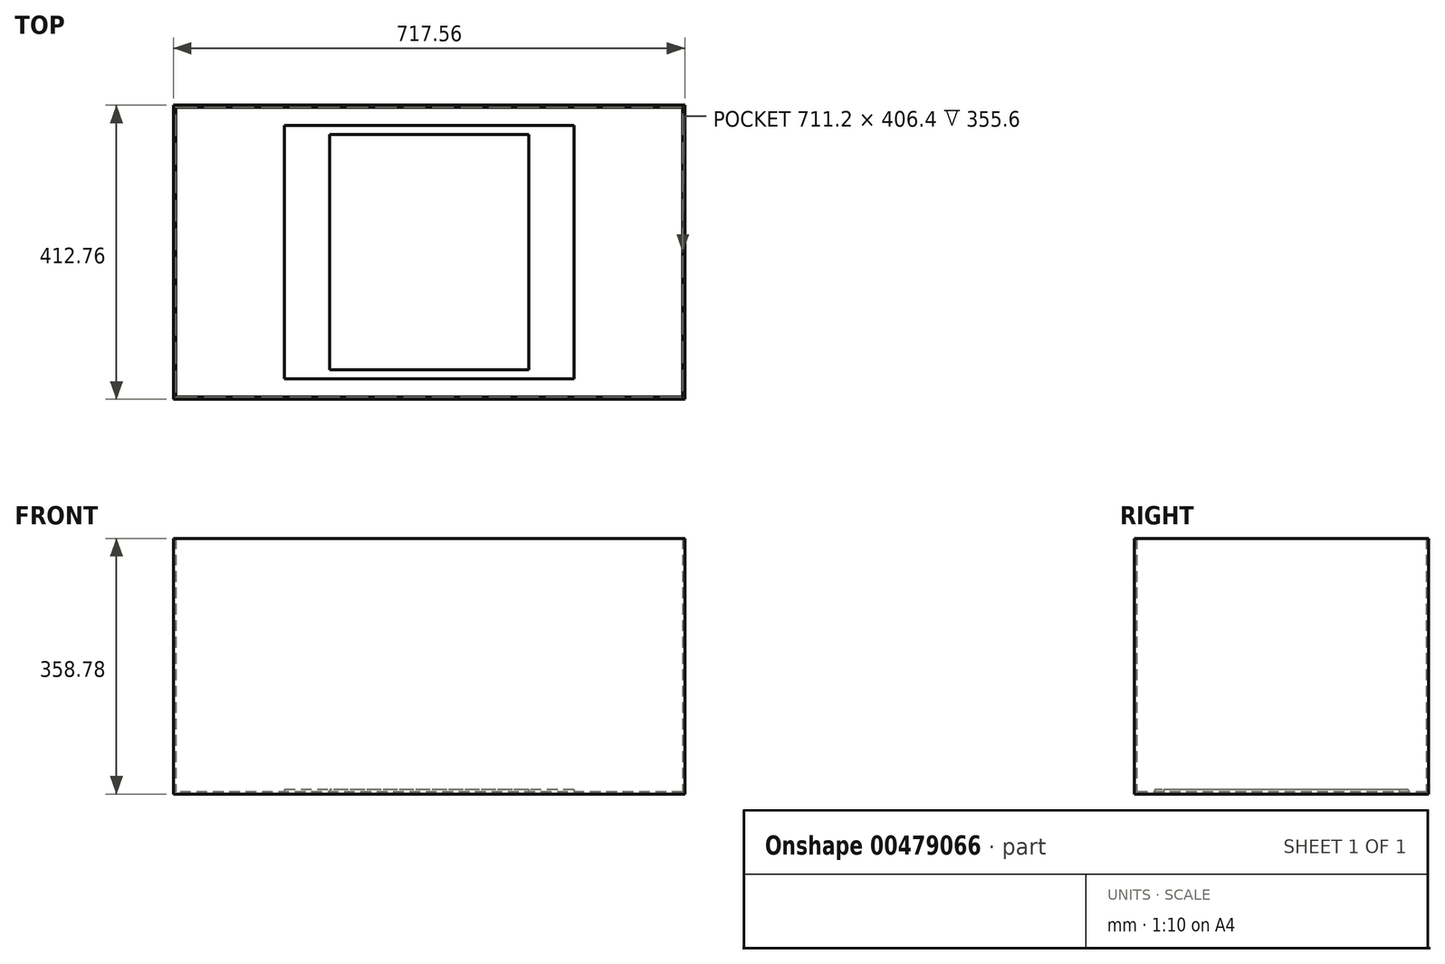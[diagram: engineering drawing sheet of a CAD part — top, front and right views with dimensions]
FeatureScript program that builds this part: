
annotation { "Feature Type Name" : "Feature", "Feature Type Description" : "" }
export const myFeature = defineFeature(function(context is Context, id is Id, definition is map)
    precondition{}
    {
        {
            var Q0;
            Q0=qCreatedBy(makeId("Top.planeOp"),FACE);
            var sketch = newSketch(context, id + "F0", { "sketchPlane" : qUnion([Q0])});
            skLineSegment(sketch, "E0.bottom", {"start": v(358.78, 206.38) * mm, "end": v(-358.78, 206.38) * mm});
            skLineSegment(sketch, "E0.top", {"start": v(358.78, -206.38) * mm, "end": v(-358.77, -206.38) * mm});
            skLineSegment(sketch, "E0.left", {"start": v(358.78, 206.38) * mm, "end": v(358.78, -206.38) * mm});
            skLineSegment(sketch, "E0.right", {"start": v(-358.78, 206.38) * mm, "end": v(-358.77, -206.38) * mm});
            skPoint(sketch, "E0.middle", {"position": v(0, 0) * mm});
            skSolve(sketch);
        }
        {
            var Q0;
            Q0 = qSketchRegion(id + "F0", true);
            extrude(context, id + "F1", {"entities" : qUnion([Q0]), "depth" : 358.77 * mm});
        }
        {
            var Q0;
            Q0=makeQuery(id+"F1.opExtrude","CAP_FACE",FACE,{"disambiguationData":[OSD([sQuery(id+"F0.wireOp",EDGE,"E0.bottom"),sQuery(id+"F0.wireOp",EDGE,"E0.top"),sQuery(id+"F0.wireOp",EDGE,"E0.left"),sQuery(id+"F0.wireOp",EDGE,"E0.right")])],"isStart":false});
            shell(context, id + "F2", {"entities" : qUnion([Q0]), "thickness" : 3.17 * mm});
        }
        {
            var Q0;
            Q0=qCreatedBy(makeId("Top.planeOp"),FACE);
            var sketch = newSketch(context, id + "F3", { "sketchPlane" : qUnion([Q0])});
            skLineSegment(sketch, "E1.bottom", {"start": v(203.2, 177.8) * mm, "end": v(-203.2, 177.8) * mm});
            skLineSegment(sketch, "E1.top", {"start": v(203.2, -177.8) * mm, "end": v(-203.2, -177.8) * mm});
            skLineSegment(sketch, "E1.left", {"start": v(203.2, 177.8) * mm, "end": v(203.2, -177.8) * mm});
            skLineSegment(sketch, "E1.right", {"start": v(-203.2, 177.8) * mm, "end": v(-203.2, -177.8) * mm});
            skPoint(sketch, "E1.middle", {"position": v(0, 0) * mm});
            skSolve(sketch);
        }
        {
            var Q0;
            Q0=makeQuery(id+"F3.imprint","IMPRINT",FACE,{"disambiguationData":[TD([[makeQuery(id+"F3.imprint","IMPRINT",EDGE,{"derivedFrom":sQuery(id+"F3.wireOp",EDGE,"E1.bottom")}),1.0]])]});
            extrude(context, id + "F4", {"entities" : qUnion([Q0]), "depth" : 6.35 * mm});
        }
        {
            var Q0;
            Q0=qCreatedBy(makeId("Top.planeOp"),FACE);
            var sketch = newSketch(context, id + "F5", { "sketchPlane" : qUnion([Q0])});
            skLineSegment(sketch, "E2.bottom", {"start": v(139.7, 165.1) * mm, "end": v(-139.7, 165.1) * mm});
            skLineSegment(sketch, "E2.top", {"start": v(139.7, -165.1) * mm, "end": v(-139.7, -165.1) * mm});
            skLineSegment(sketch, "E2.left", {"start": v(139.7, 165.1) * mm, "end": v(139.7, -165.1) * mm});
            skLineSegment(sketch, "E2.right", {"start": v(-139.7, 165.1) * mm, "end": v(-139.7, -165.1) * mm});
            skPoint(sketch, "E2.middle", {"position": v(0, 0) * mm});
            skSolve(sketch);
        }
        {
            var Q0;
            Q0=makeQuery(id+"F5.imprint","IMPRINT",FACE,{"disambiguationData":[TD([[makeQuery(id+"F5.imprint","IMPRINT",EDGE,{"derivedFrom":sQuery(id+"F5.wireOp",EDGE,"E2.bottom")}),1.0]])]});
            extrude(context, id + "F6", {"entities" : qUnion([Q0]), "depth" : 6.35 * mm});
        }
    });
